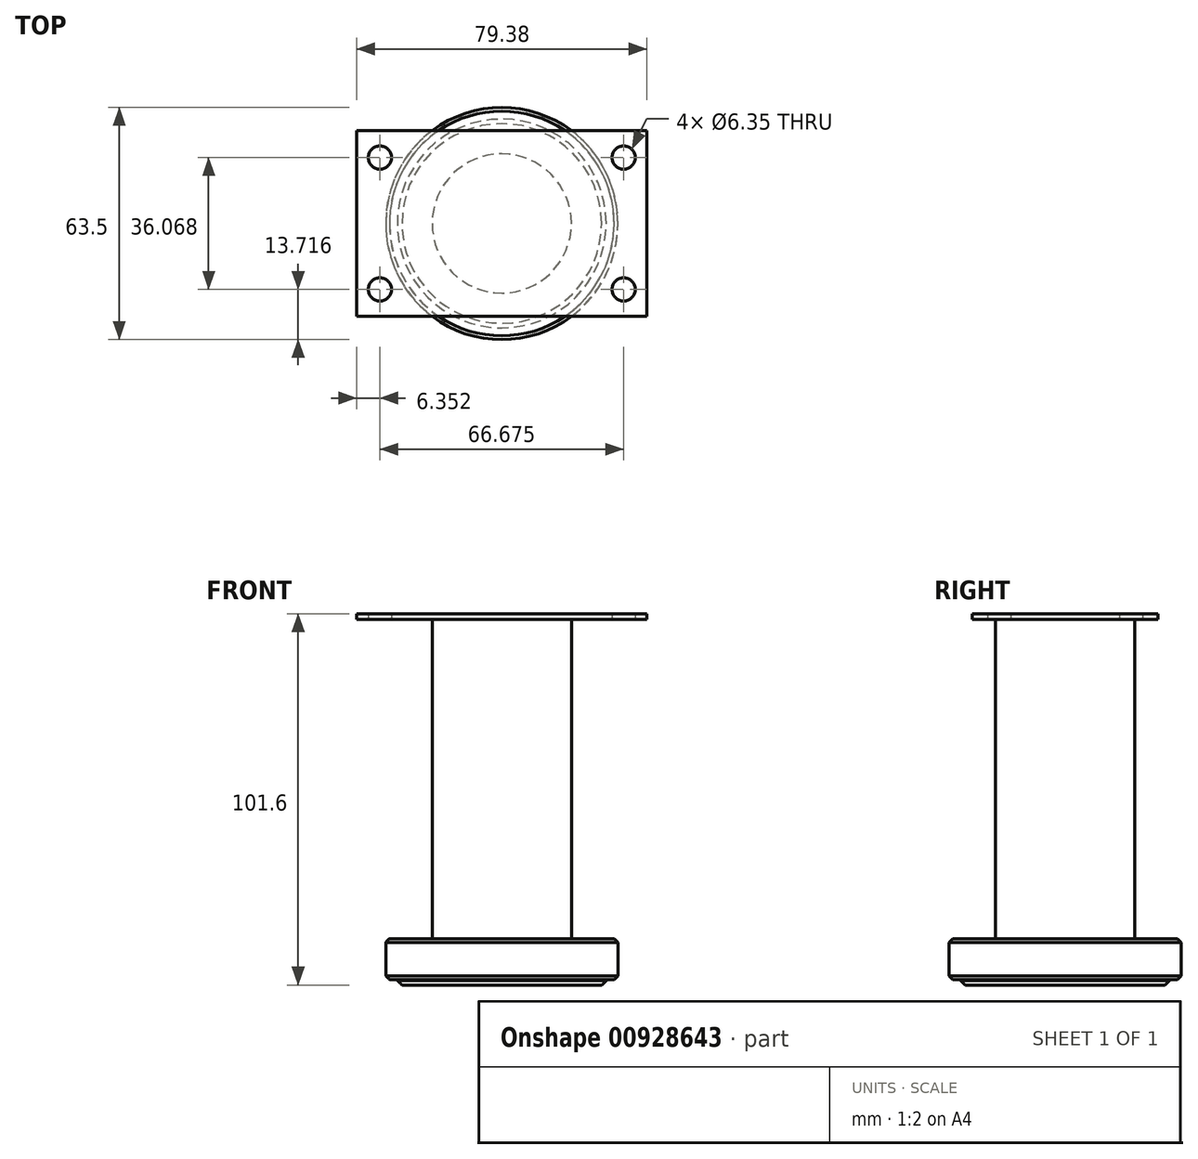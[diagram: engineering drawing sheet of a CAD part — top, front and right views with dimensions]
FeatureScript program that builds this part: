
annotation { "Feature Type Name" : "Feature", "Feature Type Description" : "" }
export const myFeature = defineFeature(function(context is Context, id is Id, definition is map)
    precondition{}
    {
        {
            var Q0;
            Q0=qCreatedBy(makeId("Top.planeOp"),FACE);
            var sketch = newSketch(context, id + "F0", { "sketchPlane" : qUnion([Q0])});
            skLineSegment(sketch, "E0.bottom", {"start": v(39.69, 25.4) * mm, "end": v(-39.69, 25.4) * mm});
            skLineSegment(sketch, "E0.top", {"start": v(39.69, -25.4) * mm, "end": v(-39.69, -25.4) * mm});
            skLineSegment(sketch, "E0.left", {"start": v(39.69, 25.4) * mm, "end": v(39.69, -25.4) * mm});
            skLineSegment(sketch, "E0.right", {"start": v(-39.69, 25.4) * mm, "end": v(-39.69, -25.4) * mm});
            skPoint(sketch, "E0.middle", {"position": v(0, 0) * mm});
            skLineSegment(sketch, "E1.bottom", {"start": v(33.34, 18.03) * mm, "end": v(-33.34, 18.03) * mm});
            skLineSegment(sketch, "E1.top", {"start": v(33.34, -18.03) * mm, "end": v(-33.34, -18.03) * mm});
            skLineSegment(sketch, "E1.left", {"start": v(33.34, 18.03) * mm, "end": v(33.34, -18.03) * mm});
            skLineSegment(sketch, "E1.right", {"start": v(-33.34, 18.03) * mm, "end": v(-33.34, -18.03) * mm});
            skCircle(sketch, "E2", {"center": v(-33.34, 18.03) * mm, "radius": 3.18 * mm});
            skCircle(sketch, "E3", {"center": v(33.34, 18.03) * mm, "radius": 3.18 * mm});
            skCircle(sketch, "E4", {"center": v(33.34, -18.03) * mm, "radius": 3.18 * mm});
            skCircle(sketch, "E5", {"center": v(-33.34, -18.03) * mm, "radius": 3.18 * mm});
            skSolve(sketch);
        }
        {
            var Q0;
            Q0=makeQuery(id+"F0.imprint","IMPRINT",FACE,{"disambiguationData":[TD([[makeQuery(id+"F0.imprint","IMPRINT",EDGE,{"derivedFrom":sQuery(id+"F0.wireOp",EDGE,"E0.bottom")}),1.0]])]});
            var Q1;
            {var subQ5=sQuery(id+"F0.wireOp",EDGE,"E3");var subQ13=sQuery(id+"F0.wireOp",EDGE,"E1.bottom");var subQ14=makeQuery(id+"F0.imprint","INTERSECT",VERTEX,{"derivedFrom":[subQ13,subQ5]});Q1=makeQuery(id+"F0.imprint","IMPRINT",FACE,{"disambiguationData":[TD([[makeQuery(id+"F0.imprint","IMPRINT",EDGE,{"disambiguationData":[TD([[subQ14,-1.0]])],"derivedFrom":subQ13}),1.0]])]});}
            extrude(context, id + "F1", {"entities" : qUnion([Q0, Q1]), "depth" : 1.52 * mm, "offsetDistance" : 25.4 * mm});
        }
        {
            var Q0;
            Q0=makeQuery(id+"F1.opExtrude","CAP_FACE",FACE,{"disambiguationData":[OSD([sQuery(id+"F0.wireOp",EDGE,"E0.bottom"),sQuery(id+"F0.wireOp",EDGE,"E0.top"),sQuery(id+"F0.wireOp",EDGE,"E0.left"),sQuery(id+"F0.wireOp",EDGE,"E0.right"),sQuery(id+"F0.wireOp",EDGE,"E2"),sQuery(id+"F0.wireOp",EDGE,"E3"),sQuery(id+"F0.wireOp",EDGE,"E4"),sQuery(id+"F0.wireOp",EDGE,"E5")])],"isStart":true});
            var sketch = newSketch(context, id + "F2", { "sketchPlane" : qUnion([Q0])});
            skCircle(sketch, "E6", {"center": v(0, 0) * mm, "radius": 19.05 * mm});
            skSolve(sketch);
        }
        {
            var Q0;
            Q0=makeQuery(id+"F2.imprint","IMPRINT",FACE,{"disambiguationData":[TD([[makeQuery(id+"F2.imprint","IMPRINT",EDGE,{"derivedFrom":sQuery(id+"F2.wireOp",EDGE,"E6")}),1.0]])]});
            extrude(context, id + "F3", {"entities" : qUnion([Q0]), "operationType" : NewBodyOperationType.ADD, "depth" : 87.38 * mm, "offsetDistance" : 25.4 * mm});
        }
        {
            var Q0;
            Q0=makeQuery(id+"F3.opExtrude","CAP_FACE",FACE,{"disambiguationData":[OSD([sQuery(id+"F2.wireOp",EDGE,"E6")])],"isStart":false});
            var sketch = newSketch(context, id + "F4", { "sketchPlane" : qUnion([Q0])});
            skCircle(sketch, "E7", {"center": v(0, 0) * mm, "radius": 31.75 * mm});
            skSolve(sketch);
        }
        {
            var Q0;
            Q0=makeQuery(id+"F4.imprint","IMPRINT",FACE,{"disambiguationData":[TD([[makeQuery(id+"F4.imprint","IMPRINT",EDGE,{"derivedFrom":sQuery(id+"F4.wireOp",EDGE,"E7")}),1.0]])]});
            var Q1;
            Q1=makeQuery(id+"F4.imprint","IMPRINT",FACE,{"disambiguationData":[TD([[makeQuery(id+"F4.imprint","IMPRINT",EDGE,{"derivedFrom":makeQuery(id+"F3.opExtrude","CAP_EDGE",EDGE,{"disambiguationData":[OSD([sQuery(id+"F2.wireOp",EDGE,"E6")])],"isStart":false})}),1.0]])]});
            extrude(context, id + "F5", {"entities" : qUnion([Q0, Q1]), "operationType" : NewBodyOperationType.ADD, "depth" : 11.18 * mm, "offsetDistance" : 25.4 * mm});
        }
        {
            var Q0;
            Q0=makeQuery(id+"F5.opExtrude","CAP_EDGE",EDGE,{"disambiguationData":[OSD([sQuery(id+"F4.wireOp",EDGE,"E7")])],"isStart":true});
            var Q1;
            Q1=makeQuery(id+"F5.opExtrude","CAP_EDGE",EDGE,{"disambiguationData":[OSD([sQuery(id+"F4.wireOp",EDGE,"E7")])],"isStart":false});
            chamfer(context, id + "F6", {"entities" : qUnion([Q0, Q1]), "width" : 1.02 * mm, "tangentPropagation" : true});
        }
        {
            var Q0;
            Q0=makeQuery(id+"F5.opExtrude","CAP_FACE",FACE,{"disambiguationData":[OSD([sQuery(id+"F4.wireOp",EDGE,"E7")])],"isStart":false});
            var sketch = newSketch(context, id + "F7", { "sketchPlane" : qUnion([Q0])});
            skCircle(sketch, "E8", {"center": v(0, 0) * mm, "radius": 28.58 * mm});
            skSolve(sketch);
        }
        {
            var Q0;
            Q0=makeQuery(id+"F7.imprint","IMPRINT",FACE,{"disambiguationData":[TD([[makeQuery(id+"F7.imprint","IMPRINT",EDGE,{"derivedFrom":sQuery(id+"F7.wireOp",EDGE,"E8")}),1.0]])]});
            extrude(context, id + "F8", {"entities" : qUnion([Q0]), "operationType" : NewBodyOperationType.ADD, "depth" : 1.52 * mm, "offsetDistance" : 25.4 * mm});
        }
        {
            var Q0;
            Q0=makeQuery(id+"F8.opExtrude","CAP_EDGE",EDGE,{"disambiguationData":[OSD([sQuery(id+"F7.wireOp",EDGE,"E8")])],"isStart":false});
            chamfer(context, id + "F9", {"entities" : qUnion([Q0]), "width" : 1.27 * mm, "tangentPropagation" : true});
        }
    });
